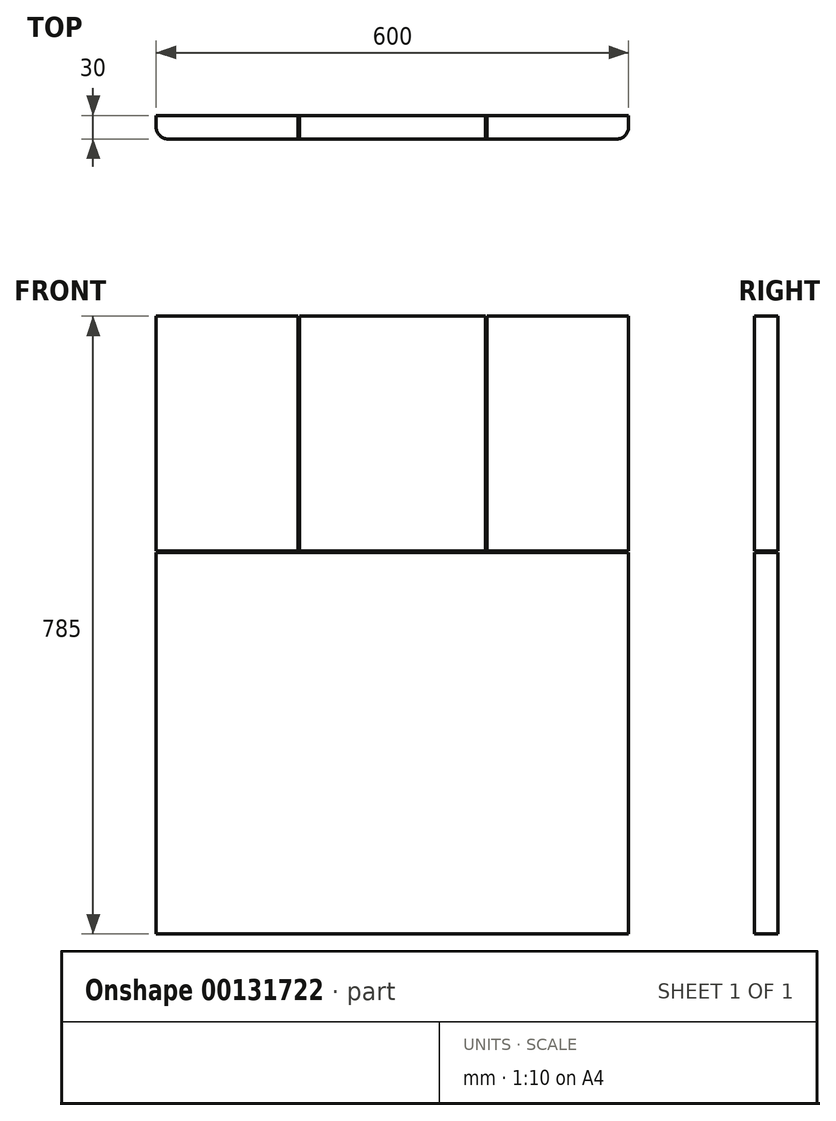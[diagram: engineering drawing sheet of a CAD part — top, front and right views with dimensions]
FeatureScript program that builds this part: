
annotation { "Feature Type Name" : "Feature", "Feature Type Description" : "" }
export const myFeature = defineFeature(function(context is Context, id is Id, definition is map)
    precondition{}
    {
        {
            var Q0;
            Q0=qCreatedBy(makeId("Front.planeOp"),FACE);
            var sketch = newSketch(context, id + "F0", { "sketchPlane" : qUnion([Q0])});
            skLineSegment(sketch, "E0.bottom", {"start": v(-300, -425) * mm, "end": v(300, -425) * mm, "construction": true});
            skLineSegment(sketch, "E0.top", {"start": v(-300, 425) * mm, "end": v(300, 425) * mm, "construction": true});
            skLineSegment(sketch, "E0.left", {"start": v(-300, -425) * mm, "end": v(-300, 425) * mm, "construction": true});
            skLineSegment(sketch, "E0.right", {"start": v(300, -425) * mm, "end": v(300, 425) * mm, "construction": true});
            skPoint(sketch, "E0.middle", {"position": v(0, 0) * mm});
            skLineSegment(sketch, "E1", {"start": v(-300, 400) * mm, "end": v(300, 400) * mm, "construction": true});
            skLineSegment(sketch, "E2", {"start": v(-300, -385) * mm, "end": v(300, -385) * mm, "construction": true});
            skLineSegment(sketch, "E3", {"start": v(0, 473.12) * mm, "end": v(0, -459.06) * mm, "construction": true});
            skPoint(sketch, "E3.startSnap0", {"position": v(0, 425) * mm});
            skPoint(sketch, "E3.endSnap0", {"position": v(0, -425) * mm});
            skLineSegment(sketch, "E4", {"start": v(-300, 100) * mm, "end": v(300, 100) * mm, "construction": true});
            skLineSegment(sketch, "E5", {"start": v(-300, 0) * mm, "end": v(300, 0) * mm, "construction": true});
            skLineSegment(sketch, "E6", {"start": v(120, 400) * mm, "end": v(120, 100) * mm, "construction": true});
            skLineSegment(sketch, "E7.MirrorCS", {"start": v(-120, 400) * mm, "end": v(-120, 100) * mm, "construction": true});
            skLineSegment(sketch, "E8", {"start": v(-224.85, 350) * mm, "end": v(228.06, 350) * mm, "construction": true});
            skLineSegment(sketch, "E9", {"start": v(-90.6, -50) * mm, "end": v(93.8, -50) * mm, "construction": true});
            skLineSegment(sketch, "E10.bottom", {"start": v(-300, 100) * mm, "end": v(300, 100) * mm});
            skLineSegment(sketch, "E10.top", {"start": v(-300, -385) * mm, "end": v(300, -385) * mm});
            skLineSegment(sketch, "E10.left", {"start": v(-300, 100) * mm, "end": v(-300, -385) * mm});
            skLineSegment(sketch, "E10.right", {"start": v(300, 100) * mm, "end": v(300, -385) * mm});
            skLineSegment(sketch, "E11.bottom", {"start": v(-300, 102) * mm, "end": v(-120, 102) * mm});
            skLineSegment(sketch, "E11.top", {"start": v(-300, 400) * mm, "end": v(-120, 400) * mm});
            skLineSegment(sketch, "E11.left", {"start": v(-300, 102) * mm, "end": v(-300, 400) * mm});
            skLineSegment(sketch, "E11.right", {"start": v(-120, 102) * mm, "end": v(-120, 400) * mm});
            skLineSegment(sketch, "E12.bottom", {"start": v(120, 102) * mm, "end": v(300, 102) * mm});
            skLineSegment(sketch, "E12.top", {"start": v(120, 400) * mm, "end": v(300, 400) * mm});
            skLineSegment(sketch, "E12.left", {"start": v(120, 102) * mm, "end": v(120, 400) * mm});
            skLineSegment(sketch, "E12.right", {"start": v(300, 102) * mm, "end": v(300, 400) * mm});
            skLineSegment(sketch, "E13.bottom", {"start": v(-118, 102) * mm, "end": v(118, 102) * mm});
            skLineSegment(sketch, "E13.top", {"start": v(-118, 400) * mm, "end": v(118, 400) * mm});
            skLineSegment(sketch, "E13.left", {"start": v(-118, 102) * mm, "end": v(-118, 400) * mm});
            skLineSegment(sketch, "E13.right", {"start": v(118, 102) * mm, "end": v(118, 400) * mm});
            skPoint(sketch, "E14", {"position": v(-120, 400) * mm});
            skPoint(sketch, "E15", {"position": v(-300, 400) * mm});
            skPoint(sketch, "E16", {"position": v(120, 400) * mm});
            skPoint(sketch, "E17", {"position": v(300, 400) * mm});
            skLineSegment(sketch, "E18", {"start": v(-210, 389.68) * mm, "end": v(-210, 229.18) * mm, "construction": true});
            skLineSegment(sketch, "E19.MirrorCS", {"start": v(210, 389.68) * mm, "end": v(210, 229.18) * mm, "construction": true});
            skSolve(sketch);
        }
        {
            var Q0;
            Q0 = qSketchRegion(id + "F0", true);
            extrude(context, id + "F1", {"entities" : qUnion([Q0]), "depth" : 30 * mm});
        }
        {
            var Q0;
            Q0=makeQuery(id+"F1.opExtrude","CAP_EDGE",EDGE,{"disambiguationData":[OSD([sQuery(id+"F0.wireOp",EDGE,"E11.left")])],"isStart":false});
            var Q1;
            Q1=makeQuery(id+"F1.opExtrude","CAP_EDGE",EDGE,{"disambiguationData":[OSD([sQuery(id+"F0.wireOp",EDGE,"E10.left")])],"isStart":false});
            var Q2;
            Q2=makeQuery(id+"F1.opExtrude","CAP_EDGE",EDGE,{"disambiguationData":[OSD([sQuery(id+"F0.wireOp",EDGE,"E12.right")])],"isStart":false});
            var Q3;
            Q3=makeQuery(id+"F1.opExtrude","CAP_EDGE",EDGE,{"disambiguationData":[OSD([sQuery(id+"F0.wireOp",EDGE,"E10.right")])],"isStart":false});
            fillet(context, id + "F2", {"entities" : qUnion([Q0, Q1, Q2, Q3]), "radius" : 15 * mm, "tangentPropagation" : true, "allowEdgeOverflow" : false});
        }
    });
